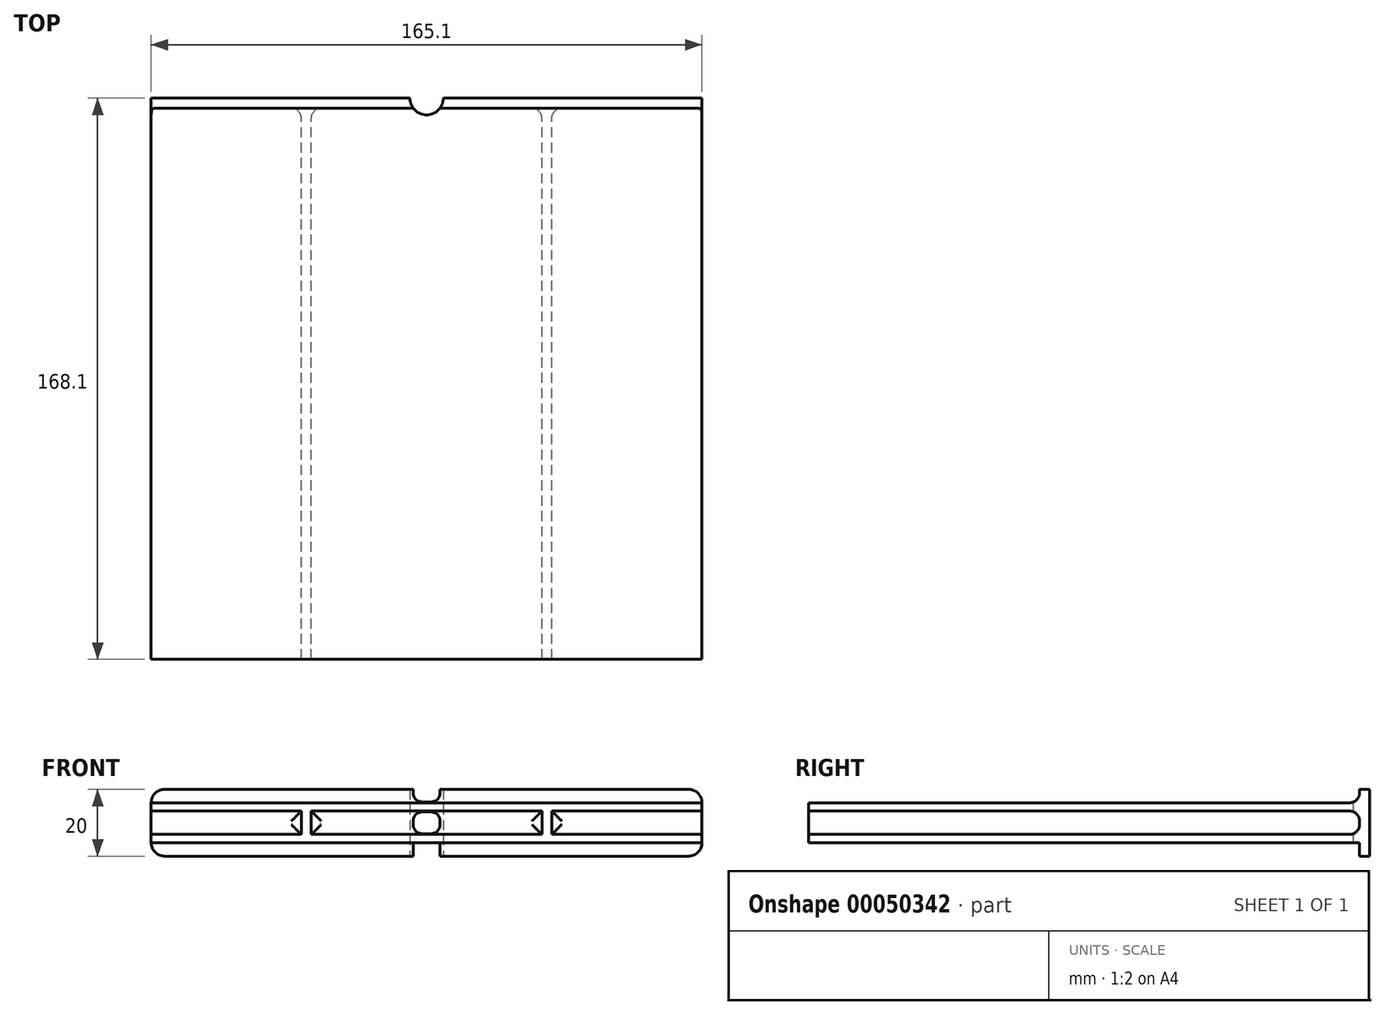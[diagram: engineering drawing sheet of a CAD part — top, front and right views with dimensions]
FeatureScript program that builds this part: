
annotation { "Feature Type Name" : "Feature", "Feature Type Description" : "" }
export const myFeature = defineFeature(function(context is Context, id is Id, definition is map)
    precondition{}
    {
        {
            var Q0;
            Q0=qCreatedBy(makeId("Front.planeOp"),FACE);
            var sketch = newSketch(context, id + "F0", { "sketchPlane" : qUnion([Q0])});
            skLineSegment(sketch, "E0.bottom", {"start": v(0, 0) * mm, "end": v(-45, 0) * mm});
            skLineSegment(sketch, "E0.top", {"start": v(0, -2.5) * mm, "end": v(-165.1, -2.5) * mm});
            skLineSegment(sketch, "E0.left", {"start": v(0, 0) * mm, "end": v(0, -2.5) * mm});
            skLineSegment(sketch, "E0.right", {"start": v(-165.1, 0) * mm, "end": v(-165.1, -2.5) * mm});
            skLineSegment(sketch, "E1.left", {"start": v(-120.1, 0) * mm, "end": v(-120.1, 7) * mm});
            skLineSegment(sketch, "E1.right", {"start": v(-117.1, 0) * mm, "end": v(-117.1, 7) * mm});
            skLineSegment(sketch, "E2.left", {"start": v(-48, 0) * mm, "end": v(-48, 7) * mm});
            skLineSegment(sketch, "E2.right", {"start": v(-45, 0) * mm, "end": v(-45, 7) * mm});
            skLineSegment(sketch, "E3.bottom", {"start": v(0, 7) * mm, "end": v(-45, 7) * mm});
            skLineSegment(sketch, "E3.top", {"start": v(0, 9.5) * mm, "end": v(-165.1, 9.5) * mm});
            skLineSegment(sketch, "E3.left", {"start": v(0, 7) * mm, "end": v(0, 9.5) * mm});
            skLineSegment(sketch, "E3.right", {"start": v(-165.1, 7) * mm, "end": v(-165.1, 9.5) * mm});
            skLineSegment(sketch, "E4.trimOffspring", {"start": v(-48, 7) * mm, "end": v(-117.1, 7) * mm});
            skLineSegment(sketch, "E5.trimOffspring", {"start": v(-48, 0) * mm, "end": v(-117.1, 0) * mm});
            skLineSegment(sketch, "E6.trimOffspring", {"start": v(-120.1, 7) * mm, "end": v(-165.1, 7) * mm});
            skLineSegment(sketch, "E7.trimOffspring", {"start": v(-120.1, 0) * mm, "end": v(-165.1, 0) * mm});
            skSolve(sketch);
        }
        {
            var Q0;
            Q0=makeQuery(id+"F0.imprint","IMPRINT",FACE,{"disambiguationData":[TD([[makeQuery(id+"F0.imprint","IMPRINT",EDGE,{"derivedFrom":sQuery(id+"F0.wireOp",EDGE,"E0.bottom")}),1.0]])]});
            extrude(context, id + "F1", {"entities" : qUnion([Q0]), "depth" : 165.1 * mm});
        }
        {
            var Q0;
            Q0=makeQuery(id+"F1.opExtrude","CAP_FACE",FACE,{"disambiguationData":[OSD([sQuery(id+"F0.wireOp",EDGE,"E0.bottom"),sQuery(id+"F0.wireOp",EDGE,"E0.top"),sQuery(id+"F0.wireOp",EDGE,"E0.left"),sQuery(id+"F0.wireOp",EDGE,"E0.right"),sQuery(id+"F0.wireOp",EDGE,"E1.left"),sQuery(id+"F0.wireOp",EDGE,"E1.right"),sQuery(id+"F0.wireOp",EDGE,"E2.left"),sQuery(id+"F0.wireOp",EDGE,"E2.right"),sQuery(id+"F0.wireOp",EDGE,"E3.bottom"),sQuery(id+"F0.wireOp",EDGE,"E3.top"),sQuery(id+"F0.wireOp",EDGE,"E3.left"),sQuery(id+"F0.wireOp",EDGE,"E3.right"),sQuery(id+"F0.wireOp",EDGE,"E4.trimOffspring"),sQuery(id+"F0.wireOp",EDGE,"E5.trimOffspring"),sQuery(id+"F0.wireOp",EDGE,"E6.trimOffspring"),sQuery(id+"F0.wireOp",EDGE,"E7.trimOffspring")])],"isStart":true});
            var sketch = newSketch(context, id + "F2", { "sketchPlane" : qUnion([Q0])});
            skLineSegment(sketch, "E8.bottom", {"start": v(161.1, -6.5) * mm, "end": v(4, -6.5) * mm});
            skLineSegment(sketch, "E8.top", {"start": v(161.1, 13.5) * mm, "end": v(4, 13.5) * mm});
            skLineSegment(sketch, "E8.left", {"start": v(165.1, -2.5) * mm, "end": v(165.1, 9.5) * mm});
            skLineSegment(sketch, "E8.right", {"start": v(0, -2.5) * mm, "end": v(0, 9.5) * mm});
            skPoint(sketch, "E9.visualSharp", {"position": v(0, 13.5) * mm});
            skArc(sketch, "E9.filletArc", {"start": v(4, 13.5) * mm, "mid": v(1.17, 12.33) * mm, "end": v(0, 9.5) * mm});
            skPoint(sketch, "E10.visualSharp", {"position": v(0, -6.5) * mm});
            skArc(sketch, "E10.filletArc", {"start": v(0, -2.5) * mm, "mid": v(1.17, -5.33) * mm, "end": v(4, -6.5) * mm});
            skPoint(sketch, "E11.visualSharp", {"position": v(165.1, 13.5) * mm});
            skArc(sketch, "E11.filletArc", {"start": v(165.1, 9.5) * mm, "mid": v(163.93, 12.33) * mm, "end": v(161.1, 13.5) * mm});
            skPoint(sketch, "E12.visualSharp", {"position": v(165.1, -6.5) * mm});
            skArc(sketch, "E12.filletArc", {"start": v(161.1, -6.5) * mm, "mid": v(163.93, -5.33) * mm, "end": v(165.1, -2.5) * mm});
            skSolve(sketch);
        }
        {
            var Q0;
            Q0 = qSketchRegion(id + "F2", true);
            extrude(context, id + "F3", {"entities" : qUnion([Q0]), "operationType" : NewBodyOperationType.ADD, "depth" : 3 * mm});
        }
        {
            var Q0;
            Q0=makeQuery(id+"F1.opExtrude","CAP_EDGE",EDGE,{"disambiguationData":[OSD([sQuery(id+"F0.wireOp",EDGE,"E0.top")])],"isStart":true});
            var Q1;
            Q1=makeQuery(id+"F1.opExtrude","CAP_EDGE",EDGE,{"disambiguationData":[OSD([sQuery(id+"F0.wireOp",EDGE,"E3.top")])],"isStart":true});
            fillet(context, id + "F4", {"entities" : qUnion([Q0, Q1]), "radius" : 3 * mm, "tangentPropagation" : true, "allowEdgeOverflow" : false});
        }
        {
            var Q0;
            Q0=makeQuery(id+"F1.opExtrude","CAP_EDGE",EDGE,{"disambiguationData":[OSD([sQuery(id+"F0.wireOp",EDGE,"E6.trimOffspring")])],"isStart":true});
            var Q1;
            Q1=makeQuery(id+"F1.opExtrude","CAP_EDGE",EDGE,{"disambiguationData":[OSD([sQuery(id+"F0.wireOp",EDGE,"E1.left")])],"isStart":true});
            var Q2;
            Q2=makeQuery(id+"F1.opExtrude","CAP_EDGE",EDGE,{"disambiguationData":[OSD([sQuery(id+"F0.wireOp",EDGE,"E4.trimOffspring")])],"isStart":true});
            var Q3;
            Q3=makeQuery(id+"F1.opExtrude","CAP_EDGE",EDGE,{"disambiguationData":[OSD([sQuery(id+"F0.wireOp",EDGE,"E2.left")])],"isStart":true});
            var Q4;
            Q4=makeQuery(id+"F1.opExtrude","CAP_EDGE",EDGE,{"disambiguationData":[OSD([sQuery(id+"F0.wireOp",EDGE,"E3.bottom")])],"isStart":true});
            var Q5;
            Q5=makeQuery(id+"F1.opExtrude","CAP_EDGE",EDGE,{"disambiguationData":[OSD([sQuery(id+"F0.wireOp",EDGE,"E2.right")])],"isStart":true});
            var Q6;
            Q6=makeQuery(id+"F1.opExtrude","CAP_EDGE",EDGE,{"disambiguationData":[OSD([sQuery(id+"F0.wireOp",EDGE,"E0.bottom")])],"isStart":true});
            var Q7;
            Q7=makeQuery(id+"F1.opExtrude","CAP_EDGE",EDGE,{"disambiguationData":[OSD([sQuery(id+"F0.wireOp",EDGE,"E5.trimOffspring")])],"isStart":true});
            var Q8;
            Q8=makeQuery(id+"F1.opExtrude","CAP_EDGE",EDGE,{"disambiguationData":[OSD([sQuery(id+"F0.wireOp",EDGE,"E1.right")])],"isStart":true});
            var Q9;
            Q9=makeQuery(id+"F1.opExtrude","CAP_EDGE",EDGE,{"disambiguationData":[OSD([sQuery(id+"F0.wireOp",EDGE,"E7.trimOffspring")])],"isStart":true});
            fillet(context, id + "F5", {"entities" : qUnion([Q0, Q1, Q2, Q3, Q4, Q5, Q6, Q7, Q8, Q9]), "radius" : 3 * mm, "tangentPropagation" : true, "allowEdgeOverflow" : false});
        }
        {
            var Q0;
            Q0=makeQuery(id+"F3.opExtrude","SWEPT_FACE",FACE,{"disambiguationData":[OSD([sQuery(id+"F2.wireOp",EDGE,"E8.bottom")])]});
            var sketch = newSketch(context, id + "F6", { "sketchPlane" : qUnion([Q0])});
            skArc(sketch, "E13", {"start": v(-77.55, -3) * mm, "mid": v(-82.55, 2) * mm, "end": v(-87.55, -3) * mm});
            skLineSegment(sketch, "E14", {"start": v(-87.55, -3) * mm, "end": v(-77.55, -3) * mm});
            skSolve(sketch);
        }
        {
            var Q0;
            Q0 = qSketchRegion(id + "F6", true);
            extrude(context, id + "F7", {"entities" : qUnion([Q0]), "operationType" : NewBodyOperationType.REMOVE, "endBound" : BoundingType.THROUGH_ALL, "oppositeDirection" : true, "depth" : 25 * mm});
        }
    });
